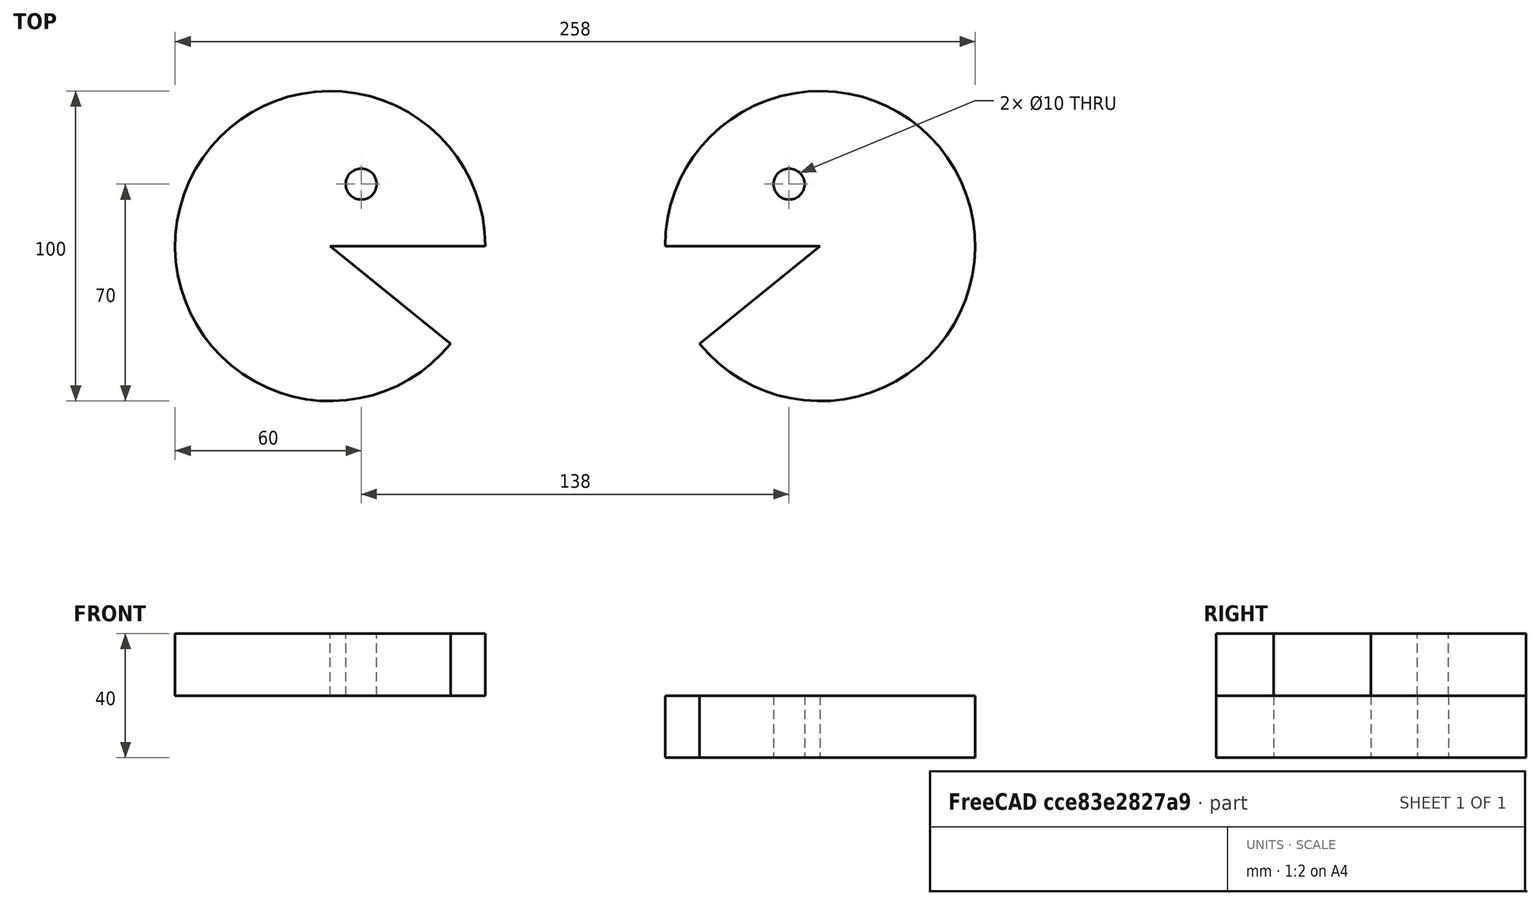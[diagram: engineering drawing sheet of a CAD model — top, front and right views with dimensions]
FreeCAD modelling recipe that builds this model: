
FCSTD DOCUMENT  (FreeCAD 0.18R16131 (Git))
Label: pacman_dani
License: All rights reserved
LicenseURL: http://en.wikipedia.org/wiki/All_rights_reserved
objects: Part::Cylinder×4, Part::Cut×2, Part::MultiFuse×1
note: 7 computed .brp shape members not serialized (recipe doc carries the construction recipe); baked Part::Feature solids carry a one-line shape summary decoded from their .brp

FEATURE [Part::Cylinder] Cylinder  label="Cilindro"
  Angle = 321
  AttacherType = Attacher::AttachEngine3D
  Height = 20
  Radius = 50
FEATURE [Part::Cylinder] Cylinder001  label="Cilindro001"
  Angle = 360
  AttacherType = Attacher::AttachEngine3D
  Height = 25
  Placement = pos=(10,20,0) rot=(0,0,1;0rad)
  Radius = 5
FEATURE [Part::Cut] Cut
  Base = -> Cylinder
  Refine = true
  Tool = -> Cylinder001
FEATURE [Part::Cylinder] Cylinder002  label="Cilindro002"
  Angle = 360
  AttacherType = Attacher::AttachEngine3D
  Height = 25
  Placement = pos=(10,20,0) rot=(0,0,1;0rad)
  Radius = 5
FEATURE [Part::Cylinder] Cylinder003  label="Cilindro003"
  Angle = 321
  AttacherType = Attacher::AttachEngine3D
  Height = 20
  Radius = 50
FEATURE [Part::Cut] Cut001
  Base = -> Cylinder003
  Placement = pos=(158,0,0) rot=(0,1,0;3.14159rad)
  Refine = true
  Tool = -> Cylinder002
FEATURE [Part::MultiFuse] Fusion
  Refine = true
  Shapes = -> [Cut,Cut001]
